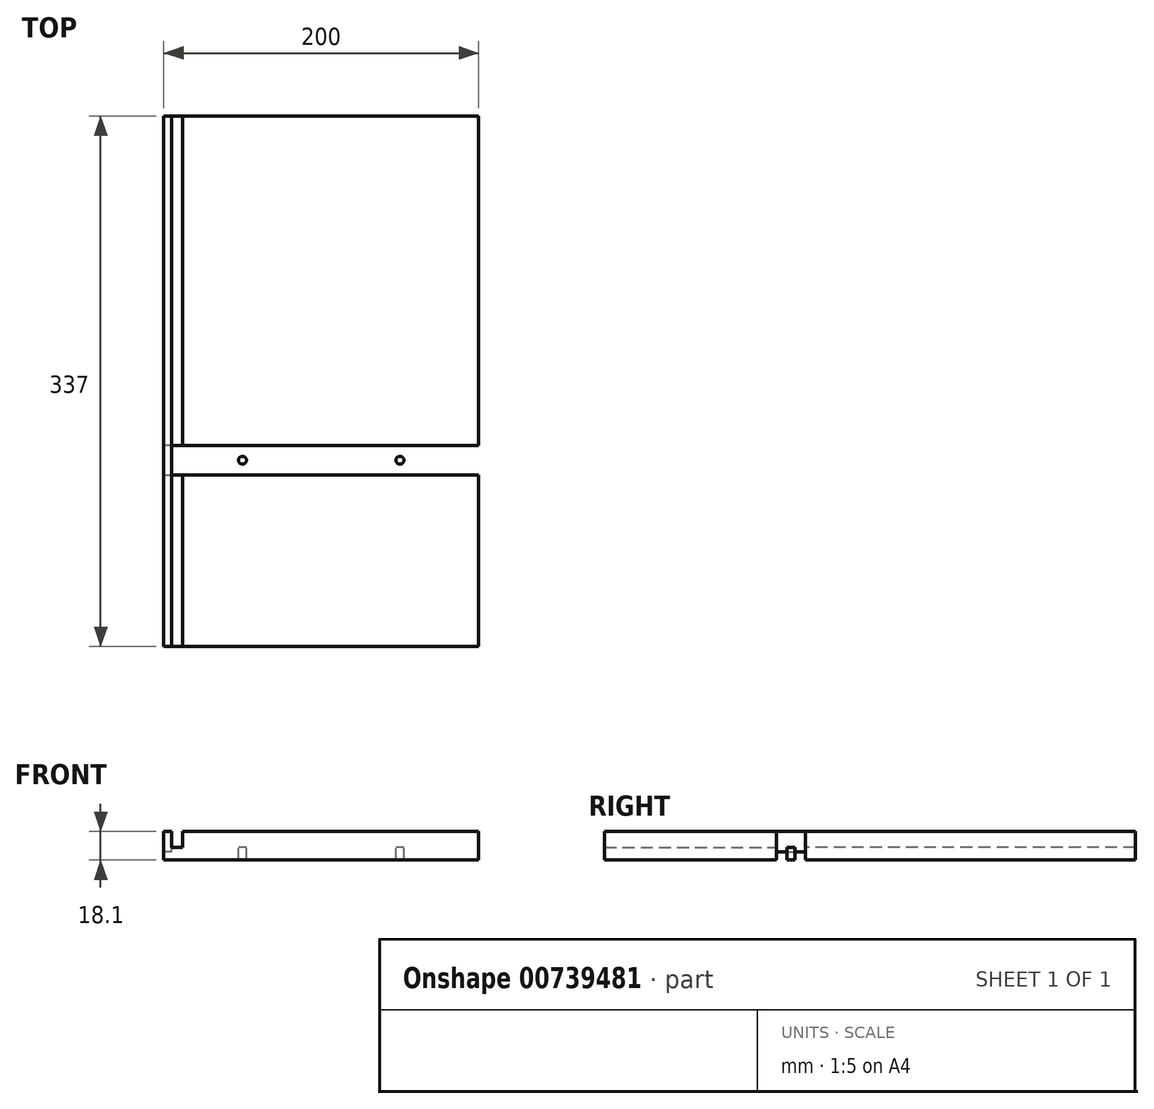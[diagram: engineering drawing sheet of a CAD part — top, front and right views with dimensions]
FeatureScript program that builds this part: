
annotation { "Feature Type Name" : "Feature", "Feature Type Description" : "" }
export const myFeature = defineFeature(function(context is Context, id is Id, definition is map)
    precondition{}
    {
        {
            var Q0;
            Q0=qCreatedBy(makeId("Top.planeOp"),FACE);
            var sketch = newSketch(context, id + "F0", { "sketchPlane" : qUnion([Q0])});
            skLineSegment(sketch, "E0.bottom", {"start": v(100, 168.5) * mm, "end": v(-100, 168.5) * mm});
            skLineSegment(sketch, "E0.top", {"start": v(100, -168.5) * mm, "end": v(-100, -168.5) * mm});
            skLineSegment(sketch, "E0.left", {"start": v(100, 168.5) * mm, "end": v(100, -168.5) * mm});
            skLineSegment(sketch, "E0.right", {"start": v(-100, 168.5) * mm, "end": v(-100, -168.5) * mm});
            skPoint(sketch, "E0.middle", {"position": v(0, 0) * mm});
            skSolve(sketch);
        }
        {
            var Q0;
            Q0=makeQuery(id+"F0.imprint","IMPRINT",FACE,{"disambiguationData":[TD([[makeQuery(id+"F0.imprint","IMPRINT",EDGE,{"derivedFrom":sQuery(id+"F0.wireOp",EDGE,"E0.bottom")}),1.0]])]});
            extrude(context, id + "F1", {"entities" : qUnion([Q0]), "depth" : 18.1 * mm, "offsetDistance" : 25 * mm});
        }
        {
            var Q0;
            Q0=makeQuery(id+"F1.opExtrude","CAP_FACE",FACE,{"disambiguationData":[OSD([sQuery(id+"F0.wireOp",EDGE,"E0.bottom"),sQuery(id+"F0.wireOp",EDGE,"E0.top"),sQuery(id+"F0.wireOp",EDGE,"E0.left"),sQuery(id+"F0.wireOp",EDGE,"E0.right")])],"isStart":false});
            var sketch = newSketch(context, id + "F2", { "sketchPlane" : qUnion([Q0])});
            skLineSegment(sketch, "E1", {"start": v(-100, -168.5) * mm, "end": v(-100, -59.5) * mm});
            skLineSegment(sketch, "E2", {"start": v(-100, -59.5) * mm, "end": v(100, -59.5) * mm});
            skLineSegment(sketch, "E3", {"start": v(100, -59.5) * mm, "end": v(100, -40.9) * mm});
            skLineSegment(sketch, "E4", {"start": v(100, -40.9) * mm, "end": v(-100, -40.9) * mm});
            skLineSegment(sketch, "E5", {"start": v(-100, -40.9) * mm, "end": v(-100, -59.5) * mm});
            skLineSegment(sketch, "E6.1.0.0", {"start": v(-75, -168.5) * mm, "end": v(-75, -59.5) * mm});
            skLineSegment(sketch, "E6.1.0.1", {"start": v(-75, -59.5) * mm, "end": v(125, -59.5) * mm});
            skLineSegment(sketch, "E6.1.0.2", {"start": v(125, -59.5) * mm, "end": v(125, -40.9) * mm});
            skLineSegment(sketch, "E6.1.0.3", {"start": v(125, -40.9) * mm, "end": v(-75, -40.9) * mm});
            skLineSegment(sketch, "E6.1.0.4", {"start": v(-75, -40.9) * mm, "end": v(-75, -59.5) * mm});
            skLineSegment(sketch, "E6.2.0.0", {"start": v(-50, -168.5) * mm, "end": v(-50, -59.5) * mm});
            skLineSegment(sketch, "E6.2.0.1", {"start": v(-50, -59.5) * mm, "end": v(150, -59.5) * mm});
            skLineSegment(sketch, "E6.2.0.2", {"start": v(150, -59.5) * mm, "end": v(150, -40.9) * mm});
            skLineSegment(sketch, "E6.2.0.3", {"start": v(150, -40.9) * mm, "end": v(-50, -40.9) * mm});
            skLineSegment(sketch, "E6.2.0.4", {"start": v(-50, -40.9) * mm, "end": v(-50, -59.5) * mm});
            skLineSegment(sketch, "E6.direction1", {"start": v(-100, -168.5) * mm, "end": v(-75, -168.5) * mm, "construction": true});
            skLineSegment(sketch, "E7", {"start": v(-100, 168.5) * mm, "end": v(-100, 158.5) * mm});
            skLineSegment(sketch, "E8", {"start": v(-100, 158.5) * mm, "end": v(-100, 139.9) * mm});
            skPoint(sketch, "E9.end.orphan", {"position": v(100, 158.5) * mm});
            skSolve(sketch);
        }
        {
            var Q0;
            Q0=qSketchRegion(id+"F2",true);
            extrude(context, id + "F3", {"entities" : qUnion([Q0]), "operationType" : NewBodyOperationType.REMOVE, "oppositeDirection" : true, "depth" : 10 * mm, "offsetDistance" : 25 * mm});
        }
        {
            var Q0;
            Q0=makeQuery(id+"F3.boolean.opBoolean","COPY",FACE,{"derivedFrom":makeQuery(id+"F3.opExtrude","CAP_FACE",FACE,{"disambiguationData":[OSD([sQuery(id+"F2.wireOp",EDGE,"E2"),sQuery(id+"F2.wireOp",EDGE,"E4"),sQuery(id+"F2.wireOp",EDGE,"E5"),sQuery(id+"F2.wireOp",EDGE,"E6.1.0.1"),sQuery(id+"F2.wireOp",EDGE,"E6.1.0.3"),sQuery(id+"F2.wireOp",EDGE,"E6.2.0.1"),sQuery(id+"F2.wireOp",EDGE,"E6.2.0.2"),sQuery(id+"F2.wireOp",EDGE,"E6.2.0.3")])],"isStart":false})});
            var sketch = newSketch(context, id + "F4", { "sketchPlane" : qUnion([Q0])});
            skLineSegment(sketch, "E10", {"start": v(-100, -50.2) * mm, "end": v(100, -50.2) * mm});
            skLineSegment(sketch, "E11", {"start": v(100, -50.2) * mm, "end": v(50, -50.2) * mm});
            skLineSegment(sketch, "E12", {"start": v(-100, -50.2) * mm, "end": v(-50, -50.2) * mm});
            skCircle(sketch, "E13", {"center": v(-50, -50.2) * mm, "radius": 2.5 * mm});
            skCircle(sketch, "E14", {"center": v(50, -50.2) * mm, "radius": 2.5 * mm});
            skSolve(sketch);
        }
        {
            var Q0;
            {var subQ0=sQuery(id+"F4.wireOp",EDGE,"E12");var subQ1=sQuery(id+"F4.wireOp",EDGE,"E10");var subQ2=makeQuery(id+"F4.imprint","INTERSECT",VERTEX,{"derivedFrom":[subQ1,subQ0]});Q0=makeQuery(id+"F4.imprint","IMPRINT",FACE,{"disambiguationData":[TD([[makeQuery(id+"F4.imprint","IMPRINT",EDGE,{"disambiguationData":[TD([[subQ2,-1.0]])],"derivedFrom":subQ1}),1.0]])]});}
            var Q1;
            {var subQ0=sQuery(id+"F4.wireOp",EDGE,"E12");var subQ1=sQuery(id+"F4.wireOp",EDGE,"E10");var subQ2=makeQuery(id+"F4.imprint","INTERSECT",VERTEX,{"derivedFrom":[subQ1,subQ0]});Q1=makeQuery(id+"F4.imprint","IMPRINT",FACE,{"disambiguationData":[TD([[makeQuery(id+"F4.imprint","IMPRINT",EDGE,{"disambiguationData":[TD([[subQ2,-1.0]])],"derivedFrom":subQ1}),-1.0]])]});}
            var Q2;
            {var subQ0=sQuery(id+"F4.wireOp",EDGE,"E11");var subQ1=sQuery(id+"F4.wireOp",EDGE,"E10");var subQ2=makeQuery(id+"F4.imprint","INTERSECT",VERTEX,{"derivedFrom":[subQ1,subQ0]});Q2=makeQuery(id+"F4.imprint","IMPRINT",FACE,{"disambiguationData":[TD([[makeQuery(id+"F4.imprint","IMPRINT",EDGE,{"disambiguationData":[TD([[subQ2,1.0]])],"derivedFrom":subQ1}),1.0]])]});}
            var Q3;
            {var subQ0=sQuery(id+"F4.wireOp",EDGE,"E11");var subQ1=sQuery(id+"F4.wireOp",EDGE,"E10");var subQ2=makeQuery(id+"F4.imprint","INTERSECT",VERTEX,{"derivedFrom":[subQ1,subQ0]});Q3=makeQuery(id+"F4.imprint","IMPRINT",FACE,{"disambiguationData":[TD([[makeQuery(id+"F4.imprint","IMPRINT",EDGE,{"disambiguationData":[TD([[subQ2,1.0]])],"derivedFrom":subQ1}),-1.0]])]});}
            extrude(context, id + "F5", {"entities" : qUnion([Q0, Q1, Q2, Q3]), "operationType" : NewBodyOperationType.REMOVE, "oppositeDirection" : true, "depth" : 25 * mm, "offsetDistance" : 25 * mm});
        }
        {
            var Q0;
            {var subQ0=sQuery(id+"F0.wireOp",EDGE,"E0.bottom");var subQ1=sQuery(id+"F0.wireOp",EDGE,"E0.right");var subQ2=sQuery(id+"F0.wireOp",EDGE,"E0.left");Q0=makeQuery(id+"F3.boolean.opBoolean","SPLIT",FACE,{"disambiguationData":[TD([makeQuery(id+"F1.opExtrude","SWEPT_FACE",FACE,{"disambiguationData":[OSD([subQ0])]})])],"derivedFrom":makeQuery(id+"F1.opExtrude","CAP_FACE",FACE,{"disambiguationData":[OSD([subQ0,sQuery(id+"F0.wireOp",EDGE,"E0.top"),subQ2,subQ1])],"isStart":false})});}
            var sketch = newSketch(context, id + "F6", { "sketchPlane" : qUnion([Q0])});
            skLineSegment(sketch, "E15", {"start": v(-100, 168.5) * mm, "end": v(-95, 168.5) * mm});
            skLineSegment(sketch, "E16", {"start": v(-95, 168.5) * mm, "end": v(-95, -40.9) * mm});
            skLineSegment(sketch, "E17", {"start": v(-95, -40.9) * mm, "end": v(-88, -40.9) * mm});
            skLineSegment(sketch, "E18", {"start": v(-88, -40.9) * mm, "end": v(-88, 168.5) * mm});
            skSolve(sketch);
        }
        {
            var Q0;
            {var subQ0=sQuery(id+"F6.wireOp",EDGE,"E16");Q0=makeQuery(id+"F6.imprint","IMPRINT",FACE,{"disambiguationData":[TD([[makeQuery(id+"F6.imprint","IMPRINT",EDGE,{"derivedFrom":subQ0}),1.0]])]});}
            extrude(context, id + "F7", {"entities" : qUnion([Q0]), "operationType" : NewBodyOperationType.REMOVE, "oppositeDirection" : true, "depth" : 10 * mm, "offsetDistance" : 25 * mm});
        }
        {
            var Q0;
            {var subQ0=sQuery(id+"F0.wireOp",EDGE,"E0.top");var subQ1=sQuery(id+"F0.wireOp",EDGE,"E0.left");var subQ2=sQuery(id+"F0.wireOp",EDGE,"E0.right");Q0=makeQuery(id+"F3.boolean.opBoolean","SPLIT",FACE,{"disambiguationData":[TD([makeQuery(id+"F1.opExtrude","SWEPT_FACE",FACE,{"disambiguationData":[OSD([subQ0])]})])],"derivedFrom":makeQuery(id+"F1.opExtrude","CAP_FACE",FACE,{"disambiguationData":[OSD([sQuery(id+"F0.wireOp",EDGE,"E0.bottom"),subQ0,subQ1,subQ2])],"isStart":false})});}
            var sketch = newSketch(context, id + "F8", { "sketchPlane" : qUnion([Q0])});
            skLineSegment(sketch, "E19", {"start": v(-100, -168.5) * mm, "end": v(-95, -168.5) * mm});
            skLineSegment(sketch, "E20", {"start": v(-95, -168.5) * mm, "end": v(-95, -59.5) * mm});
            skLineSegment(sketch, "E21", {"start": v(-95, -59.5) * mm, "end": v(-88, -59.5) * mm});
            skLineSegment(sketch, "E22", {"start": v(-88, -59.5) * mm, "end": v(-88, -168.5) * mm});
            skSolve(sketch);
        }
        {
            var Q0;
            {var subQ0=sQuery(id+"F8.wireOp",EDGE,"E20");Q0=makeQuery(id+"F8.imprint","IMPRINT",FACE,{"disambiguationData":[TD([[makeQuery(id+"F8.imprint","IMPRINT",EDGE,{"derivedFrom":subQ0}),-1.0]])]});}
            extrude(context, id + "F9", {"entities" : qUnion([Q0]), "operationType" : NewBodyOperationType.REMOVE, "oppositeDirection" : true, "depth" : 10 * mm, "offsetDistance" : 25 * mm});
        }
        {
            var Q0;
            {var subQ0=sQuery(id+"F0.wireOp",EDGE,"E0.top");var subQ1=makeQuery(id+"F1.opExtrude","SWEPT_FACE",FACE,{"disambiguationData":[OSD([subQ0])]});var subQ2=sQuery(id+"F0.wireOp",EDGE,"E0.right");var subQ3=makeQuery(id+"F1.opExtrude","SWEPT_FACE",FACE,{"disambiguationData":[OSD([subQ2])]});var subQ5=sQuery(id+"F0.wireOp",EDGE,"E0.left");Q0=makeQuery(id+"F9.boolean.opBoolean","SPLIT",FACE,{"disambiguationData":[TD([subQ3])],"derivedFrom":makeQuery(id+"F3.boolean.opBoolean","SPLIT",FACE,{"disambiguationData":[TD([subQ1])],"derivedFrom":makeQuery(id+"F1.opExtrude","CAP_FACE",FACE,{"disambiguationData":[OSD([sQuery(id+"F0.wireOp",EDGE,"E0.bottom"),subQ0,subQ5,subQ2])],"isStart":false})})});}
            var sketch = newSketch(context, id + "F10", { "sketchPlane" : qUnion([Q0])});
            skLineSegment(sketch, "E23.bottom", {"start": v(-95, -59.5) * mm, "end": v(-100, -59.5) * mm});
            skLineSegment(sketch, "E23.top", {"start": v(-95, -40.9) * mm, "end": v(-100, -40.9) * mm});
            skLineSegment(sketch, "E23.left", {"start": v(-95, -59.5) * mm, "end": v(-95, -40.9) * mm});
            skLineSegment(sketch, "E23.right", {"start": v(-100, -59.5) * mm, "end": v(-100, -40.9) * mm});
            skSolve(sketch);
        }
        {
            var Q0;
            Q0 = qSketchRegion(id + "F10", true);
            extrude(context, id + "F11", {"entities" : qUnion([Q0]), "operationType" : NewBodyOperationType.ADD, "oppositeDirection" : true, "depth" : 13 * mm, "offsetDistance" : 25 * mm});
        }
    });
